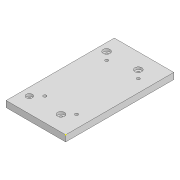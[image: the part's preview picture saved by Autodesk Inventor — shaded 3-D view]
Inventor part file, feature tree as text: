
AUTODESK INVENTOR PART (.ipt)
format: ipt  version: 2020 (Build 240168000, 168)  size: 185,856 bytes
history: native  units: mm
features: sketch x5, extrude x4, other x1
ambient origin geometry x8: Origin, YZ Plane, XZ Plane, XY Plane, X Axis, Y Axis, Z Axis, Center Point
bodies: Body1 (feature_tree)
feature tree (10):
  other  "Sólido1"
  extrude  "Extrusão1"  Depth=140.0mm
  extrude  "Extrusão2"  Depth=4.0mm
  sketch  "Esboço3"  dims[d4=4.0mm d5=4.0mm]
  extrude  "Extrusão3"  Depth=4.0mm
  extrude  "Extrusão4"  Depth=10.0mm
  sketch  "Esboço1"  dims[d0=77.0mm d1=140.0mm]
  sketch  "Esboço2"  dims[d2=4.0mm d3=4.0mm]
  sketch  "Esboço4"  dims[d6=10.0mm d7=10.0mm]
  sketch  "Esboço5"  dims[d8=20.0mm d9=20.0mm d10=20.0mm d11=20.0mm d12=26.0mm d13=26.0mm d14=8.0mm d15=0.0mm d16=8.0mm d17=9.0mm d18=9.0mm d19=9.0mm d20=3.0mm d21=0.0mm d22=4.0mm d23=4.0mm d24=10.0mm d25=10.0mm d26=10.0mm d27=10.0mm d28=4.0mm d29=4.0mm d30=10.0mm d31=10.0mm d32=10.0mm d33=10.0mm d34=12.0mm d35=0.0mm d36=6.95mm d37=6.95mm d38=6.95mm d39=6.95mm d40=5.0mm d41=0.0mm]
